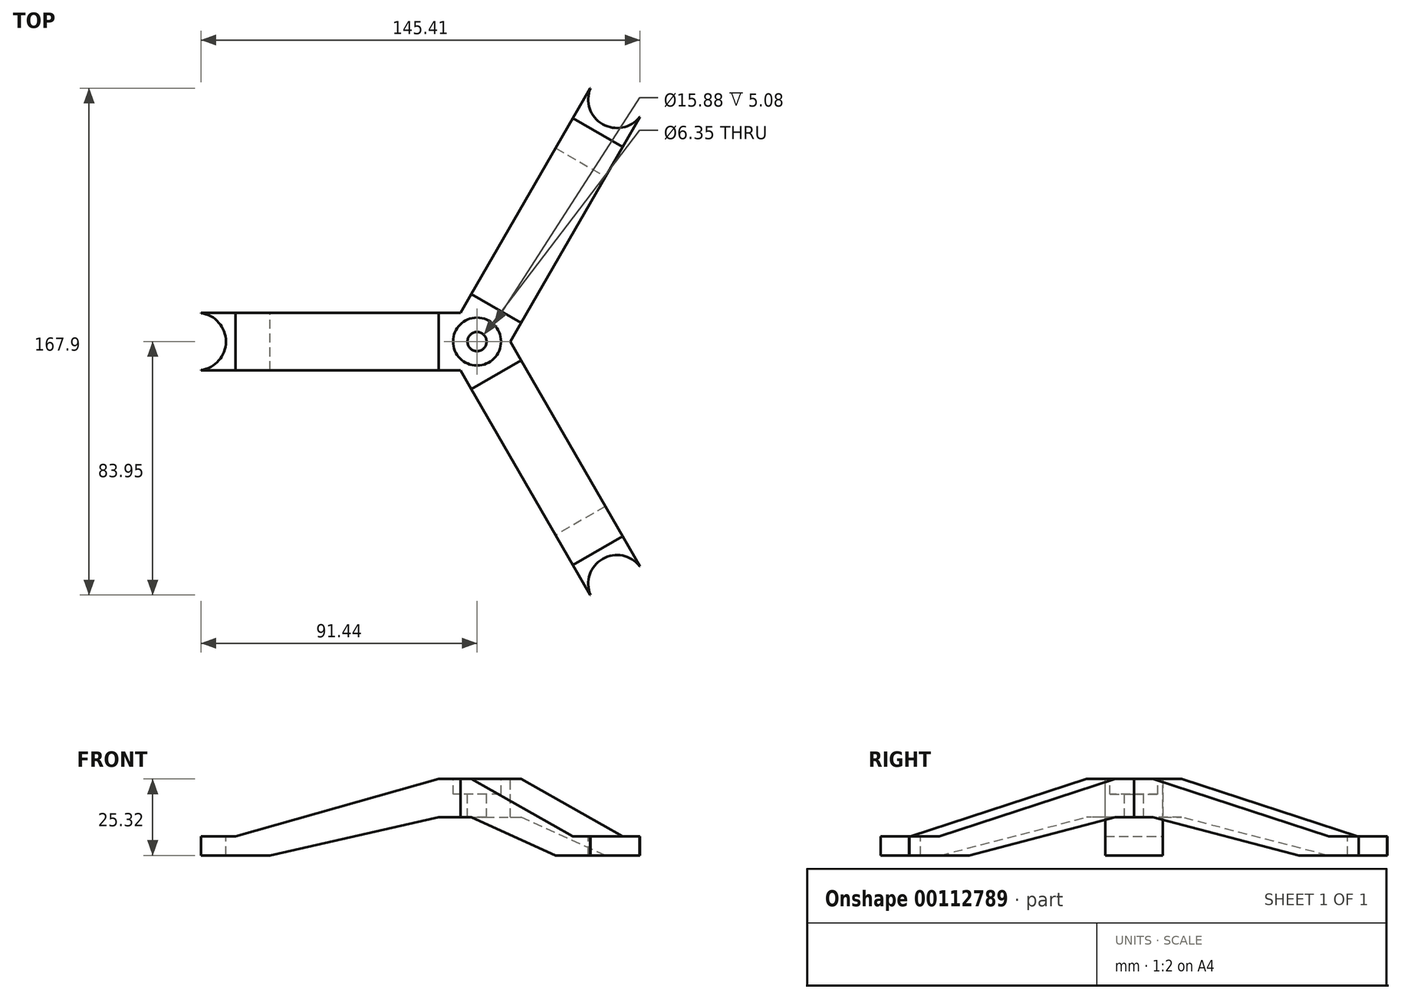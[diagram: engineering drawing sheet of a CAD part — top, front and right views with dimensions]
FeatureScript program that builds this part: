
annotation { "Feature Type Name" : "Feature", "Feature Type Description" : "" }
export const myFeature = defineFeature(function(context is Context, id is Id, definition is map)
    precondition{}
    {
        {
            var Q0;
            Q0=qCreatedBy(makeId("Front.planeOp"),FACE);
            var sketch = newSketch(context, id + "F0", { "sketchPlane" : qUnion([Q0])});
            skLineSegment(sketch, "E0.bottom", {"start": v(-68.58, 0) * mm, "end": v(-91.44, 0) * mm});
            skLineSegment(sketch, "E0.top", {"start": v(-68.58, 6.35) * mm, "end": v(-91.44, 6.35) * mm});
            skLineSegment(sketch, "E0.left", {"start": v(-68.58, 0) * mm, "end": v(-68.58, 6.35) * mm});
            skLineSegment(sketch, "E0.right", {"start": v(-91.44, 0) * mm, "end": v(-91.44, 6.35) * mm});
            skLineSegment(sketch, "E1.bottom", {"start": v(0, 12.62) * mm, "end": v(-12.7, 12.62) * mm});
            skLineSegment(sketch, "E1.top", {"start": v(0, 25.32) * mm, "end": v(-12.7, 25.32) * mm});
            skLineSegment(sketch, "E1.left", {"start": v(0, 12.62) * mm, "end": v(0, 25.32) * mm});
            skLineSegment(sketch, "E1.right", {"start": v(-12.7, 12.62) * mm, "end": v(-12.7, 25.32) * mm});
            skLineSegment(sketch, "E2", {"start": v(-80, 6.35) * mm, "end": v(-12.7, 25.32) * mm});
            skLineSegment(sketch, "E3", {"start": v(-68.58, 0) * mm, "end": v(-12.7, 12.62) * mm});
            skSolve(sketch);
        }
        {
            var Q0;
            Q0=makeQuery(id+"F0.imprint","IMPRINT",FACE,{"disambiguationData":[TD([[makeQuery(id+"F0.imprint","IMPRINT",EDGE,{"derivedFrom":sQuery(id+"F0.wireOp",EDGE,"E0.bottom")}),-1.0]])]});
            var Q1;
            {var subQ1=sQuery(id+"F0.wireOp",EDGE,"E0.left");Q1=makeQuery(id+"F0.imprint","IMPRINT",FACE,{"disambiguationData":[TD([[makeQuery(id+"F0.imprint","IMPRINT",EDGE,{"derivedFrom":subQ1}),-1.0]])]});}
            extrude(context, id + "F1", {"entities" : qUnion([Q0, Q1]), "endBound" : BoundingType.SYMMETRIC, "depth" : 19.05 * mm});
        }
        {
            var Q0;
            Q0=makeQuery(id+"F1.opExtrude","SWEPT_FACE",FACE,{"disambiguationData":[OSD([sQuery(id+"F0.wireOp",EDGE,"E0.top")])]});
            var sketch = newSketch(context, id + "F2", { "sketchPlane" : qUnion([Q0])});
            skArc(sketch, "E4", {"start": v(-91.44, -9.44) * mm, "mid": v(-83.18, 0) * mm, "end": v(-91.44, 9.44) * mm});
            skPoint(sketch, "E4.centerSnap0", {"position": v(-91.44, 0) * mm});
            skLineSegment(sketch, "E5", {"start": v(-91.44, -9.53) * mm, "end": v(-91.44, 9.53) * mm});
            skSolve(sketch);
        }
        {
            var Q0;
            {var subQ0=sQuery(id+"F2.wireOp",EDGE,"E4");var subQ1=makeQuery(id+"F1.opExtrude","SWEPT_EDGE",EDGE,{"disambiguationData":[OSD([sQuery(id+"F0.wireOp",EDGE,"E0.top"),sQuery(id+"F0.wireOp",EDGE,"E0.right")])]});var subQ2=makeQuery(id+"F2.imprint","INTERSECT",VERTEX,{"disambiguationData":[OD(0.0)],"derivedFrom":[subQ1,subQ0]});Q0=makeQuery(id+"F2.imprint","IMPRINT",FACE,{"disambiguationData":[TD([[makeQuery(id+"F2.imprint","IMPRINT",EDGE,{"disambiguationData":[TD([[subQ2,-1.0]])],"derivedFrom":subQ0}),1.0]])]});}
            extrude(context, id + "F3", {"entities" : qUnion([Q0]), "operationType" : NewBodyOperationType.REMOVE, "endBound" : BoundingType.THROUGH_ALL, "oppositeDirection" : true, "depth" : 25.4 * mm});
        }
        {
            var Q0;
            Q0=makeQuery(id+"F0.imprint","IMPRINT",FACE,{"disambiguationData":[TD([[makeQuery(id+"F0.imprint","IMPRINT",EDGE,{"derivedFrom":sQuery(id+"F0.wireOp",EDGE,"E1.bottom")}),-1.0]])]});
            extrude(context, id + "F4", {"entities" : qUnion([Q0]), "operationType" : NewBodyOperationType.ADD, "endBound" : BoundingType.SYMMETRIC, "depth" : 19.05 * mm});
        }
        {
            var Q0;
            Q0=makeQuery(id+"F4.opExtrude","SWEPT_FACE",FACE,{"disambiguationData":[OSD([sQuery(id+"F0.wireOp",EDGE,"E1.top")])]});
            var sketch = newSketch(context, id + "F5", { "sketchPlane" : qUnion([Q0])});
            skArc(sketch, "E6", {"start": v(0, 7.94) * mm, "mid": v(-7.94, 0) * mm, "end": v(0, -7.94) * mm});
            skLineSegment(sketch, "E7", {"start": v(0, -7.94) * mm, "end": v(0, 7.94) * mm});
            skSolve(sketch);
        }
        {
            var Q0;
            Q0=makeQuery(id+"F5.imprint","IMPRINT",FACE,{"disambiguationData":[TD([[makeQuery(id+"F5.imprint","IMPRINT",EDGE,{"derivedFrom":sQuery(id+"F5.wireOp",EDGE,"E6")}),1.0]])]});
            extrude(context, id + "F6", {"entities" : qUnion([Q0]), "operationType" : NewBodyOperationType.REMOVE, "oppositeDirection" : true, "depth" : 5.08 * mm});
        }
        {
            var Q0;
            Q0=makeQuery(id+"F6.boolean.opBoolean","COPY",FACE,{"derivedFrom":makeQuery(id+"F6.opExtrude","CAP_FACE",FACE,{"disambiguationData":[OSD([sQuery(id+"F5.wireOp",EDGE,"E6"),sQuery(id+"F5.wireOp",EDGE,"E7")])],"isStart":false})});
            var sketch = newSketch(context, id + "F7", { "sketchPlane" : qUnion([Q0])});
            skArc(sketch, "E8", {"start": v(0, 3.17) * mm, "mid": v(-3.17, 0) * mm, "end": v(0, -3.18) * mm});
            skLineSegment(sketch, "E9", {"start": v(0, 3.17) * mm, "end": v(0, -3.18) * mm});
            skSolve(sketch);
        }
        {
            var Q0;
            Q0 = qSketchRegion(id + "F7", true);
            extrude(context, id + "F8", {"entities" : qUnion([Q0]), "operationType" : NewBodyOperationType.REMOVE, "oppositeDirection" : true, "depth" : 25.4 * mm});
        }
        {
            var Q0;
            Q0=qCreatedBy(makeId("Front.planeOp"),FACE);
            var sketch = newSketch(context, id + "F9", { "sketchPlane" : qUnion([Q0])});
            skLineSegment(sketch, "E10", {"start": v(0, 0) * mm, "end": v(0, 38.22) * mm});
            skSolve(sketch);
        }
        {
            var Q0;
            Q0=makeQuery(id+"F1.opExtrude","SWEPT_BODY",BODY,{"disambiguationData":[OSD([sQuery(id+"F0.wireOp",EDGE,"E0.bottom"),sQuery(id+"F0.wireOp",EDGE,"E0.top"),sQuery(id+"F0.wireOp",EDGE,"E0.right"),sQuery(id+"F0.wireOp",EDGE,"E1.right"),sQuery(id+"F0.wireOp",EDGE,"E2"),sQuery(id+"F0.wireOp",EDGE,"E3")])]});
            var Q1;
            Q1=makeQuery(id+"F1.opExtrude","SWEPT_FACE",FACE,{"disambiguationData":[OSD([sQuery(id+"F0.wireOp",EDGE,"E2")])]});
            var Q2;
            {var subQ0=sQuery(id+"F0.wireOp",EDGE,"E1.right");Q2=makeQuery(id+"F4.boolean.opBoolean","MERGE",FACE,{"derivedFrom":[makeQuery(id+"F1.opExtrude","CAP_FACE",FACE,{"disambiguationData":[OSD([sQuery(id+"F0.wireOp",EDGE,"E0.bottom"),sQuery(id+"F0.wireOp",EDGE,"E0.top"),sQuery(id+"F0.wireOp",EDGE,"E0.right"),subQ0,sQuery(id+"F0.wireOp",EDGE,"E2"),sQuery(id+"F0.wireOp",EDGE,"E3")])],"isStart":false}),makeQuery(id+"F4.opExtrude","CAP_FACE",FACE,{"disambiguationData":[OSD([sQuery(id+"F0.wireOp",EDGE,"E1.bottom"),sQuery(id+"F0.wireOp",EDGE,"E1.top"),sQuery(id+"F0.wireOp",EDGE,"E1.left"),subQ0])],"isStart":false})]});}
            var Q3;
            Q3=makeQuery(id+"F4.opExtrude","SWEPT_FACE",FACE,{"disambiguationData":[OSD([sQuery(id+"F0.wireOp",EDGE,"E1.top")])]});
            var Q4;
            Q4=makeQuery(id+"F6.boolean.opBoolean","COPY",FACE,{"derivedFrom":makeQuery(id+"F6.opExtrude","SWEPT_FACE",FACE,{"disambiguationData":[OSD([sQuery(id+"F5.wireOp",EDGE,"E6")])]})});
            var Q5;
            Q5=sQuery(id+"F9.wireOp",EDGE,"E10");
            circularPattern(context, id + "F10", {"operationType" : NewBodyOperationType.ADD, "entities" : qUnion([Q0]), "axis" : qUnion([Q5]), "angle" : 360 * degree, "instanceCount" : 3, "equalSpace" : true});
        }
    });
